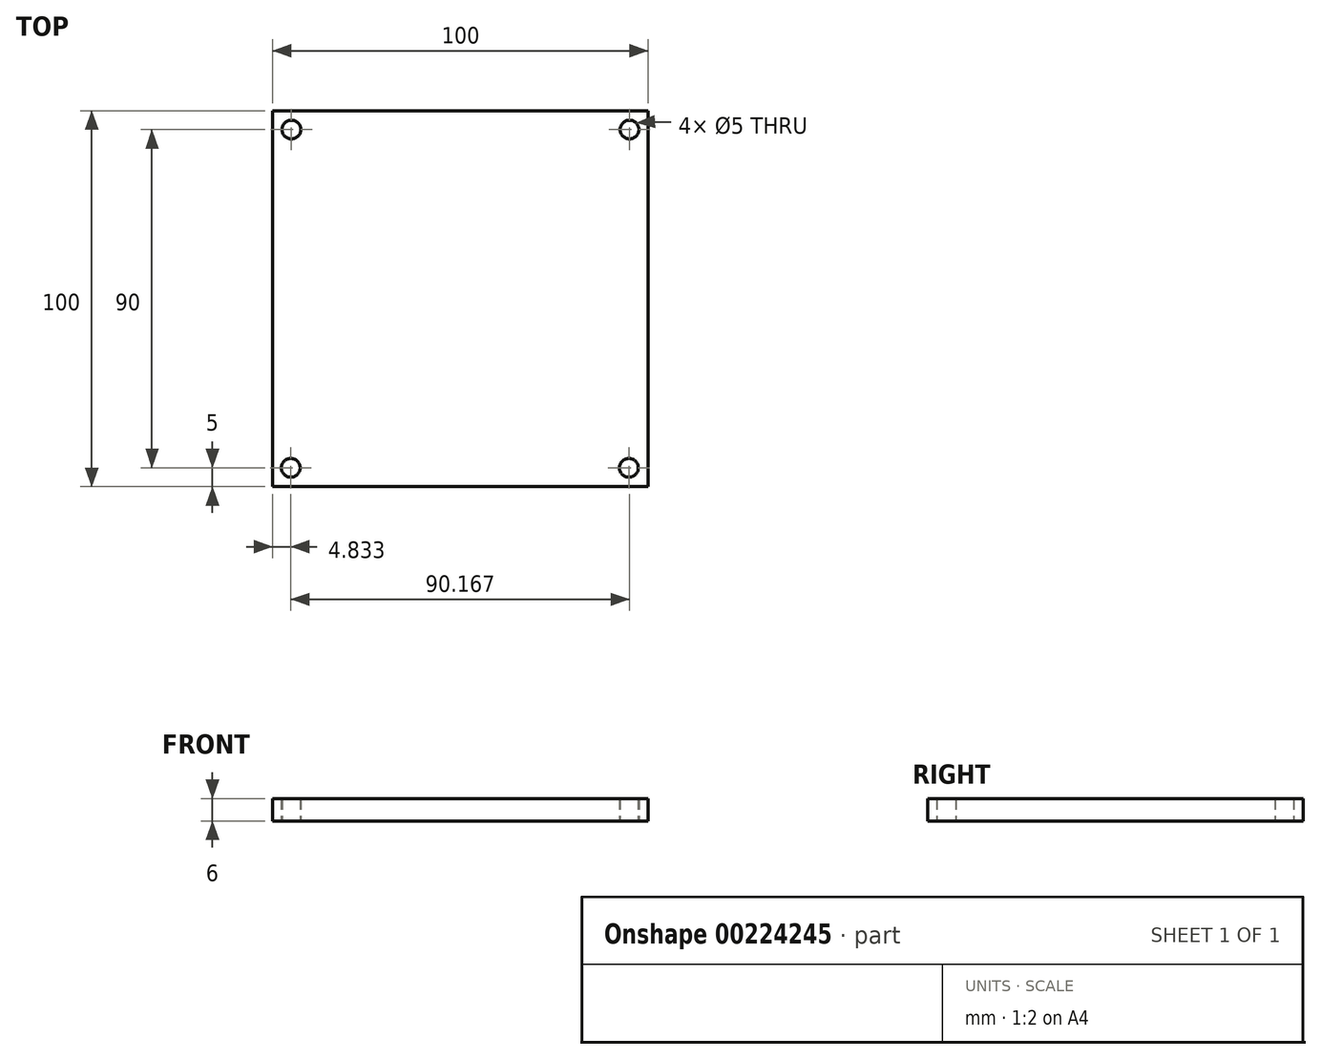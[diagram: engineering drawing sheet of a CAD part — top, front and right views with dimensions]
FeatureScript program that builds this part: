
annotation { "Feature Type Name" : "Feature", "Feature Type Description" : "" }
export const myFeature = defineFeature(function(context is Context, id is Id, definition is map)
    precondition{}
    {
        {
            var Q0;
            Q0=qCreatedBy(makeId("Top.planeOp"),FACE);
            var sketch = newSketch(context, id + "F0", { "sketchPlane" : qUnion([Q0])});
            skLineSegment(sketch, "E0.bottom", {"start": v(50, 50) * mm, "end": v(-50, 50) * mm});
            skLineSegment(sketch, "E0.top", {"start": v(50, -50) * mm, "end": v(-50, -50) * mm});
            skLineSegment(sketch, "E0.left", {"start": v(50, 50) * mm, "end": v(50, -50) * mm});
            skLineSegment(sketch, "E0.right", {"start": v(-50, 50) * mm, "end": v(-50, -50) * mm});
            skPoint(sketch, "E0.middle", {"position": v(0, 0) * mm});
            skCircle(sketch, "E1", {"center": v(45, 45) * mm, "radius": 2.5 * mm});
            skCircle(sketch, "E2", {"center": v(-45, 45) * mm, "radius": 2.5 * mm});
            skCircle(sketch, "E3", {"center": v(-45.17, -45) * mm, "radius": 2.5 * mm});
            skCircle(sketch, "E4", {"center": v(44.83, -45) * mm, "radius": 2.5 * mm});
            skSolve(sketch);
        }
        {
            var Q0;
            Q0=makeQuery(id+"F0.imprint","IMPRINT",FACE,{"disambiguationData":[TD([[makeQuery(id+"F0.imprint","IMPRINT",EDGE,{"derivedFrom":sQuery(id+"F0.wireOp",EDGE,"E0.bottom")}),1.0]])]});
            extrude(context, id + "F1", {"entities" : qUnion([Q0]), "depth" : 6 * mm});
        }
    });
